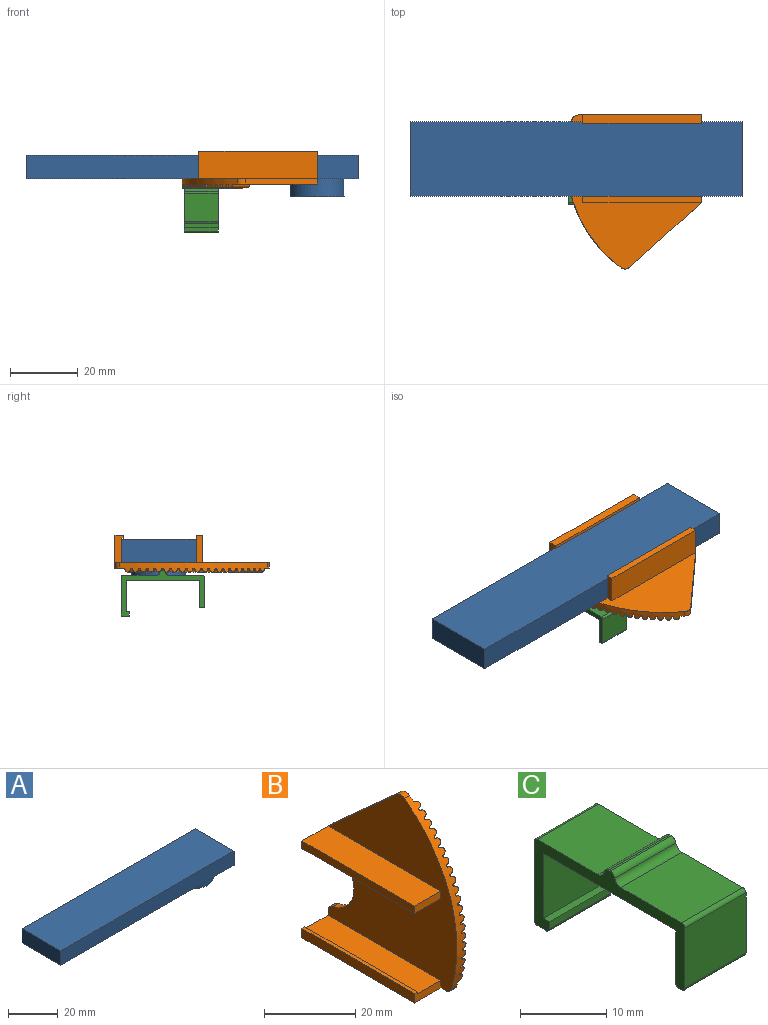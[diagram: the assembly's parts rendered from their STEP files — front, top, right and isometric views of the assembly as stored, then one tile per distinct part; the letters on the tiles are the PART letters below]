
ASSEMBLY  parts=3 mates=4
PART A: 8 faces, bbox 98.3x22x12.3 mm
  f0: plane 98.27x7mm, normal (0,-1,0), area 687.9mm2, adj f1,f3,f4,f5
  f1: plane 22x7mm, normal (1,0,0), area 154mm2, adj f0,f2,f4,f5
  f2: plane 98.27x7mm, normal (0,1,0), area 687.9mm2, adj f1,f3,f4,f5
  f3: plane 22x7mm, normal (-1,0,0), area 154mm2, adj f0,f2,f4,f5
  f4: plane 98.27x22mm, normal (0,0,1), area 2162mm2, adj f0,f1,f2,f3
  f5: plane 98.27x22mm, normal (0,0,-1), area 1960.9mm2, adj f0,f1,f2,f3,f6
  f6: cylinder r=8mm len=16mm, axis (0,0,1), area 266.4mm2, adj f5,f7
  f7: plane 16x16mm, normal (0,0,-1), area 201.1mm2, adj f6
PART B: 121 faces, bbox 10.9x40x45.6 mm
  f0: cylinder r=40mm len=43.8mm, axis (-1,0,0), area 112.4mm2, adj f2,f8,f10,f11,f12,f13,f15,f16
  f1: plane 35x7.2mm, normal (0,0,1), area 252mm2, adj f3,f8,f109,f115
  f2: plane 45.61x39.99mm, normal (1,0,0), area 1019.8mm2, adj f0,f3,f4,f5,f6,f7,f9,f12
  f3: plane 9.7x3.2mm, normal (0,1,0), area 21.8mm2, adj f1,f2,f7,f8,f110,f115,f116,f117
  f4: cylinder r=8mm len=15.68mm, axis (-1,0,0), area 35.1mm2, adj f2,f8,f117,f118
  f5: plane 9.7x3.2mm, normal (0,1,0), area 21.3mm2, adj f2,f6,f8,f111,f112,f114,f118
  f6: plane 21.18x19.09mm, normal (0,0.67,0.74), area 45.6mm2, adj f2,f5,f8,f119
  f7: plane 36.37x9.7mm, normal (0,0,-1), area 341.7mm2, adj f2,f3,f8,f109,f110,f120
  f8: plane 45.61x40mm, normal (-1,0,0), area 1195.3mm2, adj f0,f1,f3,f4,f5,f6,f7,f109
  f9: plane 1.8x1.16mm, normal (0,1,0), area 1.3mm2, adj f2,f10,f11,f12,f13
  f10: cylinder r=1mm len=8.03mm, axis (0,1,-0.02), area 10.8mm2, adj f0,f9,f11,f13
  f11: cylinder r=1mm len=8.03mm, axis (0,-1,-0.02), area 10.8mm2, adj f0,f9,f10,f12
  f12: cylinder r=0.2mm len=8mm, axis (0,1,0.02), area 2.5mm2, adj f0,f2,f9,f11
  f13: cylinder r=0.2mm len=8mm, axis (0,-1,0.02), area 2.5mm2, adj f0,f2,f9,f10
  f14: plane 1.75x1.16mm, normal (0,0.97,0.23), area 1.3mm2, adj f2,f15,f16,f17,f18
  f15: cylinder r=1mm len=8.02mm, axis (0,0.98,0.21), area 10.8mm2, adj f0,f14,f16,f18
  f16: cylinder r=1mm len=7.98mm, axis (0,-0.97,-0.25), area 10.8mm2, adj f0,f14,f15,f17
  f17: cylinder r=0.2mm len=7.79mm, axis (0,0.97,0.25), area 2.5mm2, adj f0,f2,f14,f16
  f18: cylinder r=0.2mm len=7.87mm, axis (0,-0.98,-0.21), area 2.5mm2, adj f0,f2,f14,f15
  f19: plane 1.78x1.16mm, normal (0,0.98,0.17), area 1.3mm2, adj f2,f20,f21,f22,f23
  f20: cylinder r=1mm len=8.06mm, axis (0,0.99,0.15), area 10.8mm2, adj f0,f19,f21,f23
  f21: cylinder r=1mm len=8.03mm, axis (0,-0.98,-0.2), area 10.8mm2, adj f0,f19,f20,f22
  f22: cylinder r=0.2mm len=7.89mm, axis (0,0.98,0.2), area 2.5mm2, adj f0,f2,f19,f21
  f23: cylinder r=0.2mm len=7.94mm, axis (0,-0.99,-0.15), area 2.5mm2, adj f0,f2,f19,f20
  f24: plane 1.79x1.16mm, normal (0,0.99,0.12), area 1.3mm2, adj f2,f25,f26,f27,f28
  f25: cylinder r=1mm len=8.06mm, axis (0,1,0.09), area 10.8mm2, adj f0,f24,f26,f28
  f26: cylinder r=1mm len=8.06mm, axis (0,-0.99,-0.14), area 10.8mm2, adj f0,f24,f25,f27
  f27: cylinder r=0.2mm len=7.95mm, axis (0,0.99,0.14), area 2.5mm2, adj f0,f2,f24,f26
  f28: cylinder r=0.2mm len=7.99mm, axis (0,-1,-0.09), area 2.5mm2, adj f0,f2,f24,f25
  f29: plane 1.8x1.16mm, normal (0,1,0.06), area 1.3mm2, adj f2,f30,f31,f32,f33
  f30: cylinder r=1mm len=8.04mm, axis (0,1,0.04), area 10.8mm2, adj f0,f29,f31,f33
  f31: cylinder r=1mm len=8.06mm, axis (0,-1,-0.08), area 10.8mm2, adj f0,f29,f30,f32
  f32: cylinder r=0.2mm len=7.99mm, axis (0,1,0.08), area 2.5mm2, adj f0,f2,f29,f31
  f33: cylinder r=0.2mm len=8mm, axis (0,-1,-0.04), area 2.5mm2, adj f0,f2,f29,f30
  f34: plane 1.8x1.16mm, normal (0,1,-0.06), area 1.3mm2, adj f2,f35,f36,f37,f38
  f35: cylinder r=1mm len=8.06mm, axis (0,1,-0.08), area 10.8mm2, adj f0,f34,f36,f38
  f36: cylinder r=1mm len=8.04mm, axis (0,-1,0.04), area 10.8mm2, adj f0,f34,f35,f37
  f37: cylinder r=0.2mm len=8mm, axis (0,1,-0.04), area 2.5mm2, adj f0,f2,f34,f36
  f38: cylinder r=0.2mm len=7.99mm, axis (0,-1,0.08), area 2.5mm2, adj f0,f2,f34,f35
  f39: plane 1.79x1.16mm, normal (0,0.99,-0.12), area 1.3mm2, adj f2,f40,f41,f42,f43
  f40: cylinder r=1mm len=8.06mm, axis (0,0.99,-0.14), area 10.8mm2, adj f0,f39,f41,f43
  f41: cylinder r=1mm len=8.06mm, axis (0,-1,0.09), area 10.8mm2, adj f0,f39,f40,f42
  f42: cylinder r=0.2mm len=7.99mm, axis (0,1,-0.09), area 2.5mm2, adj f0,f2,f39,f41
  f43: cylinder r=0.2mm len=7.95mm, axis (0,-0.99,0.14), area 2.5mm2, adj f0,f2,f39,f40
  f44: plane 1.78x1.16mm, normal (0,0.98,-0.17), area 1.3mm2, adj f2,f45,f46,f47,f48
  f45: cylinder r=1mm len=8.03mm, axis (0,0.98,-0.2), area 10.8mm2, adj f0,f44,f46,f48
  f46: cylinder r=1mm len=8.06mm, axis (0,-0.99,0.15), area 10.8mm2, adj f0,f44,f45,f47
  f47: cylinder r=0.2mm len=7.94mm, axis (0,0.99,-0.15), area 2.5mm2, adj f0,f2,f44,f46
  f48: cylinder r=0.2mm len=7.89mm, axis (0,-0.98,0.2), area 2.5mm2, adj f0,f2,f44,f45
  f49: plane 1.75x1.16mm, normal (0,0.97,-0.23), area 1.3mm2, adj f2,f50,f51,f52,f53
  f50: cylinder r=1mm len=7.98mm, axis (0,0.97,-0.25), area 10.8mm2, adj f0,f49,f51,f53
  f51: cylinder r=1mm len=8.02mm, axis (0,-0.98,0.21), area 10.8mm2, adj f0,f49,f50,f52
  f52: cylinder r=0.2mm len=7.87mm, axis (0,0.98,-0.21), area 2.5mm2, adj f0,f2,f49,f51
  f53: cylinder r=0.2mm len=7.79mm, axis (0,-0.97,0.25), area 2.5mm2, adj f0,f2,f49,f50
  f54: plane 1.73x1.16mm, normal (0,0.96,-0.29), area 1.3mm2, adj f2,f55,f56,f57,f58
  f55: cylinder r=1mm len=7.9mm, axis (0,0.95,-0.31), area 10.8mm2, adj f0,f54,f56,f58
  f56: cylinder r=1mm len=7.96mm, axis (0,-0.96,0.27), area 10.8mm2, adj f0,f54,f55,f57
  f57: cylinder r=0.2mm len=7.77mm, axis (0,0.96,-0.27), area 2.5mm2, adj f0,f2,f54,f56
  f58: cylinder r=0.2mm len=7.68mm, axis (0,-0.95,0.31), area 2.5mm2, adj f0,f2,f54,f55
  f59: plane 1.69x1.16mm, normal (0,0.94,-0.34), area 1.3mm2, adj f2,f60,f61,f62,f63
  f60: cylinder r=1mm len=7.79mm, axis (0,0.93,-0.36), area 10.8mm2, adj f0,f59,f61,f63
  f61: cylinder r=1mm len=7.87mm, axis (0,-0.95,0.32), area 10.8mm2, adj f0,f59,f60,f62
  f62: cylinder r=0.2mm len=7.64mm, axis (0,0.95,-0.32), area 2.5mm2, adj f0,f2,f59,f61
  f63: cylinder r=0.2mm len=7.53mm, axis (0,-0.93,0.36), area 2.5mm2, adj f0,f2,f59,f60
  f64: plane 1.66x1.16mm, normal (0,0.92,-0.4), area 1.3mm2, adj f2,f65,f66,f67,f68
  f65: cylinder r=1mm len=7.65mm, axis (0,0.91,-0.42), area 10.8mm2, adj f0,f64,f66,f68
  f66: cylinder r=1mm len=7.76mm, axis (0,-0.93,0.38), area 10.8mm2, adj f0,f64,f65,f67
  f67: cylinder r=0.2mm len=7.49mm, axis (0,0.93,-0.38), area 2.5mm2, adj f0,f2,f64,f66
  f68: cylinder r=0.2mm len=7.36mm, axis (0,-0.91,0.42), area 2.5mm2, adj f0,f2,f64,f65
  f69: plane 1.61x1.16mm, normal (0,0.89,-0.45), area 1.3mm2, adj f2,f70,f71,f72,f73
  f70: cylinder r=1mm len=7.49mm, axis (0,0.88,-0.47), area 10.8mm2, adj f0,f69,f71,f73
  f71: cylinder r=1mm len=7.62mm, axis (0,-0.9,0.43), area 10.8mm2, adj f0,f69,f70,f72
  f72: cylinder r=0.2mm len=7.31mm, axis (0,0.9,-0.43), area 2.5mm2, adj f0,f2,f69,f71
  f73: cylinder r=0.2mm len=7.16mm, axis (0,-0.88,0.47), area 2.5mm2, adj f0,f2,f69,f70
  f74: plane 1.56x1.16mm, normal (0,0.87,-0.5), area 1.3mm2, adj f2,f75,f76,f77,f78
  f75: cylinder r=1mm len=7.31mm, axis (0,0.85,-0.52), area 10.8mm2, adj f0,f74,f76,f78
  f76: cylinder r=1mm len=7.45mm, axis (0,-0.88,0.48), area 10.8mm2, adj f0,f74,f75,f77
  f77: cylinder r=0.2mm len=7.11mm, axis (0,0.88,-0.48), area 2.5mm2, adj f0,f2,f74,f76
  f78: cylinder r=0.2mm len=6.94mm, axis (0,-0.85,0.52), area 2.5mm2, adj f0,f2,f74,f75
  f79: plane 1.51x1.16mm, normal (0,0.84,-0.55), area 1.3mm2, adj f2,f80,f81,f82,f83
  f80: cylinder r=1mm len=7.1mm, axis (0,0.82,-0.57), area 10.8mm2, adj f0,f79,f81,f83
  f81: cylinder r=1mm len=7.26mm, axis (0,-0.85,0.53), area 10.8mm2, adj f0,f79,f80,f82
  f82: cylinder r=0.2mm len=6.89mm, axis (0,0.85,-0.53), area 2.5mm2, adj f0,f2,f79,f81
  f83: cylinder r=0.2mm len=6.7mm, axis (0,-0.82,0.57), area 2.5mm2, adj f0,f2,f79,f80
  f84: plane 1.45x1.16mm, normal (0,0.8,-0.6), area 1.3mm2, adj f2,f85,f86,f87,f88
  f85: cylinder r=1mm len=6.86mm, axis (0,0.79,-0.61), area 10.8mm2, adj f0,f84,f86,f88
  f86: cylinder r=1mm len=7.04mm, axis (0,-0.81,0.58), area 10.8mm2, adj f0,f84,f85,f87
  f87: cylinder r=0.2mm len=6.64mm, axis (0,0.81,-0.58), area 2.5mm2, adj f0,f2,f84,f86
  f88: cylinder r=0.2mm len=6.44mm, axis (0,-0.79,0.61), area 2.5mm2, adj f0,f2,f84,f85
  f89: plane 1.38x1.16mm, normal (0,0.77,-0.64), area 1.3mm2, adj f2,f90,f91,f92,f93
  f90: cylinder r=1mm len=6.6mm, axis (0,0.75,-0.66), area 10.8mm2, adj f0,f89,f91,f93
  f91: cylinder r=1mm len=6.8mm, axis (0,-0.78,0.63), area 10.8mm2, adj f0,f89,f90,f92
  f92: cylinder r=0.2mm len=6.37mm, axis (0,0.78,-0.63), area 2.5mm2, adj f0,f2,f89,f91
  f93: cylinder r=0.2mm len=6.15mm, axis (0,-0.75,0.66), area 2.5mm2, adj f0,f2,f89,f90
  f94: plane 1.31x1.24mm, normal (0,0.73,-0.69), area 1.3mm2, adj f2,f95,f96,f97,f98
  f95: cylinder r=1mm len=6.32mm, axis (0,0.71,-0.7), area 10.8mm2, adj f0,f94,f96,f98
  f96: cylinder r=1mm len=6.54mm, axis (0,-0.74,0.67), area 10.8mm2, adj f0,f94,f95,f97
  f97: cylinder r=0.2mm len=6.07mm, axis (0,0.74,-0.67), area 2.5mm2, adj f0,f2,f94,f96
  f98: cylinder r=0.2mm len=5.84mm, axis (0,-0.71,0.7), area 2.5mm2, adj f0,f2,f94,f95
  f99: plane 1.31x1.24mm, normal (0,0.69,-0.73), area 1.3mm2, adj f2,f100,f101,f102,f103
  f100: cylinder r=1mm len=6.54mm, axis (0,0.67,-0.74), area 10.8mm2, adj f0,f99,f101,f103
  f101: cylinder r=1mm len=6.32mm, axis (0,-0.7,0.71), area 10.8mm2, adj f0,f99,f100,f102
  f102: cylinder r=0.2mm len=5.84mm, axis (0,0.7,-0.71), area 2.5mm2, adj f0,f2,f99,f101
  f103: cylinder r=0.2mm len=6.07mm, axis (0,-0.67,0.74), area 2.5mm2, adj f0,f2,f99,f100
  f104: plane 1.38x1.16mm, normal (0,0.64,-0.77), area 1.3mm2, adj f2,f105,f106,f107,f108
  f105: cylinder r=1mm len=6.8mm, axis (0,0.63,-0.78), area 10.8mm2, adj f0,f104,f106,f108
  f106: cylinder r=1mm len=6.6mm, axis (0,-0.66,0.75), area 10.8mm2, adj f0,f104,f105,f107
  f107: cylinder r=0.2mm len=6.15mm, axis (0,0.66,-0.75), area 2.5mm2, adj f0,f2,f104,f106
  f108: cylinder r=0.2mm len=6.37mm, axis (0,-0.63,0.78), area 2.5mm2, adj f0,f2,f104,f105
  f109: plane 8.1x2.5mm, normal (0,-1,0), area 16.6mm2, adj f1,f7,f8,f110,f115,f116
  f110: plane 35x2.5mm, normal (-1,0,0), area 87.5mm2, adj f3,f7,f109,f116
  f111: plane 35x8.1mm, normal (0,0,1), area 283.5mm2, adj f5,f8,f113,f114
  f112: plane 35x8.1mm, normal (0,0,-1), area 283.5mm2, adj f5,f8,f113,f114
  f113: plane 8.1x2mm, normal (0,-1,0), area 16.2mm2, adj f8,f111,f112,f114
  f114: plane 35x2mm, normal (-1,0,0), area 70mm2, adj f5,f111,f112,f113
  f115: plane 35x0.5mm, normal (1,0,0), area 17.5mm2, adj f1,f3,f109,f116
  f116: plane 35x0.9mm, normal (0,0,1), area 31.5mm2, adj f3,f109,f110,f115
  f117: cylinder r=2mm len=1.96mm, axis (-1,0,0), area 4.4mm2, adj f2,f3,f4,f8
  f118: cylinder r=2mm len=1.96mm, axis (-1,0,0), area 4.4mm2, adj f2,f4,f5,f8
  f119: cylinder r=2mm len=2.52mm, axis (-1,0,0), area 4.4mm2, adj f0,f2,f6,f8
  f120: cylinder r=2mm len=1.91mm, axis (-1,0,0), area 4.1mm2, adj f0,f2,f7,f8
PART C: 24 faces, bbox 10x24.7x13.7 mm
  f0: plane 10x9.98mm, normal (0,0,1), area 99.8mm2, adj f11,f12,f17,f20
  f1: plane 10x9.2mm, normal (0,-1,0), area 92mm2, adj f2,f10,f11,f12
  f2: plane 10x1mm, normal (0,0,1), area 10mm2, adj f1,f3,f11,f12
  f3: plane 10x1mm, normal (0,-1,0), area 10mm2, adj f2,f11,f12,f18
  f4: plane 10x1.5mm, normal (0,0,-1), area 15mm2, adj f11,f12,f18,f19
  f5: plane 11.2x10mm, normal (0,1,0), area 112mm2, adj f11,f12,f19,f20
  f6: plane 10x9.98mm, normal (0,0,1), area 99.8mm2, adj f11,f12,f16,f21
  f7: plane 10x8.5mm, normal (0,-1,0), area 85mm2, adj f11,f12,f21,f22
  f8: plane 10x0.5mm, normal (0,0,-1), area 5mm2, adj f11,f12,f22,f23
  f9: plane 10x7.5mm, normal (0,1,0), area 75mm2, adj f10,f11,f12,f23
  f10: plane 21.7x10mm, normal (0,0,-1), area 217mm2, adj f1,f9,f11,f12
  f11: plane 24.7x13.7mm, normal (1,0,0), area 69.1mm2, adj f0,f1,f2,f3,f4,f5,f6,f7
  f12: plane 24.7x13.7mm, normal (-1,0,0), area 69.1mm2, adj f0,f1,f2,f3,f4,f5,f6,f7
  f13: plane 10x0.2mm, normal (0,0,1), area 2mm2, adj f11,f12,f14,f15
  f14: cylinder r=0.8mm len=10mm, axis (-1,0,0), area 11.2mm2, adj f11,f12,f13,f16
  f15: cylinder r=0.8mm len=10mm, axis (1,0,0), area 11.2mm2, adj f11,f12,f13,f17
  f16: cylinder r=1mm len=10mm, axis (-1,0,0), area 14mm2, adj f6,f11,f12,f14
  f17: cylinder r=1mm len=10mm, axis (1,0,0), area 14mm2, adj f0,f11,f12,f15
  f18: cylinder r=0.5mm len=10mm, axis (1,0,0), area 7.9mm2, adj f3,f4,f11,f12
  f19: cylinder r=0.5mm len=10mm, axis (-1,0,0), area 7.9mm2, adj f4,f5,f11,f12
  f20: cylinder r=0.5mm len=10mm, axis (1,0,0), area 7.9mm2, adj f0,f5,f11,f12
  f21: cylinder r=0.5mm len=10mm, axis (-1,0,0), area 7.9mm2, adj f6,f7,f11,f12
  f22: cylinder r=0.5mm len=10mm, axis (-1,0,0), area 7.9mm2, adj f7,f8,f11,f12
  f23: cylinder r=0.5mm len=10mm, axis (-1,0,0), area 7.9mm2, adj f8,f9,f11,f12
PLACE A t=(-24.73,-30.91,-3.36)mm
PLACE B rot(axis=(0.58,0.58,-0.58),120deg) t=(12.33,-30.91,-3.36)mm
PLACE C t=(-21.97,-44.4,-16.66)mm
MATE planar B.f8 <-> A.f5  axis (0,0,1) through (-9.41,-37.89,-3.36)mm
MATE planar C.f10 <-> A.f6  axis (0,0,-1) through (-21.97,-32.05,-8.66)mm
MATE planar B.f1 <-> A.f2  axis (0,-1,0) through (-5.17,-19.91,0.24)mm
MATE cylindrical B.f4 <-> A.f6  axis (0,0,1) through (12.33,-30.91,-4.16)mm
